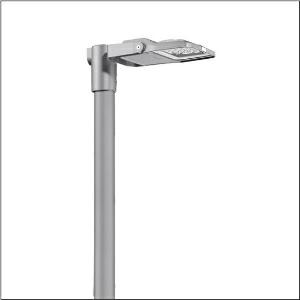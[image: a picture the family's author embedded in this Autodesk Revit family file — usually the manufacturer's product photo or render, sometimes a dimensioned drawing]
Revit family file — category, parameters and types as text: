
# Revit family: floodlight_fl_21_iq_micro___pl52_5xa7762a2d3a_f78f
name_source: partatom
category: Lighting Fixtures
units: mm (PartAtom-declared; Revit-internal decimal feet)

## family parameters
Cut with Voids When Loaded = No
Host = Face
Light Source = No
Part Type = Normal
Room Calculation Point = No
Round Connector Dimension = Use Diameter
Shared = No

## types (1)
- --- (1 x LED, 2890 lm, 23.1 W, 3000K)
    Apparent Load = 23 VA
    CIE Flux Codes = 26 60 98 100 100
    Color Rendering = 70
    Color Temperature = 3000K
    Default Elevation = 1800 mm
    Description = Floodlight FL 21 iQ micro, floodlight, primary light control with lens, of PMMA, primary optical cover: protective disc, of toughened safety glass, transparent, light distribution: PL52, light emission: direct distribution, installation type: surface-mounted, LED, High Power LED, rated luminous flux: 2.890lm, luminous efficacy: 125lm/W, light colour: 730, colour temperature: 3000K, control: Auto-Match, Temp-Guard, Night-Set, Smart-Wire, Desk-Remote (wireless, voltage-free reading and setting of iQ features in the workshop via application-optimized NFC function/RFID function), optimised constant luminous flux control (CLO 2.0), Street-Remote, with terminal, 6-pole, mains connection: 220..240V, AC, 50/60Hz, start of lifetime: 23W, end of service life: 24W, reduction: 11W, luminaire housing, of diecast aluminium, powder-coated, Siteco® metallic grey (DB 702S), corrosivity category C5 mid according to DIN EN ISO 12944, sealing non-destructively replaceable, please order mast flange separately, mast bracket, of steel, galvanised, powder-coated, Siteco® metallic grey (DB 702S), protection rating (complete): IP66, insulation class (complete): insulation class II (safety insulation), certification: CE, ENEC, VDE, protection symbol: D, impact resistance: IK07, permissible operating ambient temperature: -40..+40°C, permissible operating ambient temperature for outdoor applications: -40..+50°C, standard: DIN EN 12944, LABS conformity tested according to VDMA 24364:2018-05, packaging unit: 1 piece

Light Distribution: PL52
    Height = 65 mm
    Lamp = 1 x LED
    Lamp Light Flux = 2890 lm
    Lamp Power = 23.1 W
    Lamp count = 1
    Length = 312 mm
    Luminous efficacy = 125 lm/W
    Manufacturer = Siteco
    ModVariant = No
    Model = 5XA7762A2D3A
    Number of Poles = 1
    OnlyDefault = Yes
    Power Factor = 1
    Product Name = Floodlight FL 21 iQ micro | PL52
    Product group = floodlight | pylon annexe
    ProductGroupID = 6200
    Protection Class = Protection class II
    Protection Degree = IP 66
    RLX_Detail_Level = 1
    RLX_Emergency_Light_Flux = 0 lm
    RLX_Emergency_Type = 0
    RLX_Emergency_Type_DB = No
    RlxData = <blob elided: 101813 chars, md5=fc459ed4>
    Socket = socket
    Standby Power = 0 W
    System Light Flux = 2890 lm
    System Power = 23 W
    Type Comments = factory setting: luminous flux: 100 % | dim-lin: 254 | 455 mA
    Type Image = l_1007121.jpg
    URL = http://relux.com
    VarID = @adj_149131
    Voltage = 0 V
    Weight = 0.00 kg
    Width = 230 mm

## geometry (parser evidence)
native form markers: Blend x4, Sweep x13
no freeform markers — native parametric forms only
